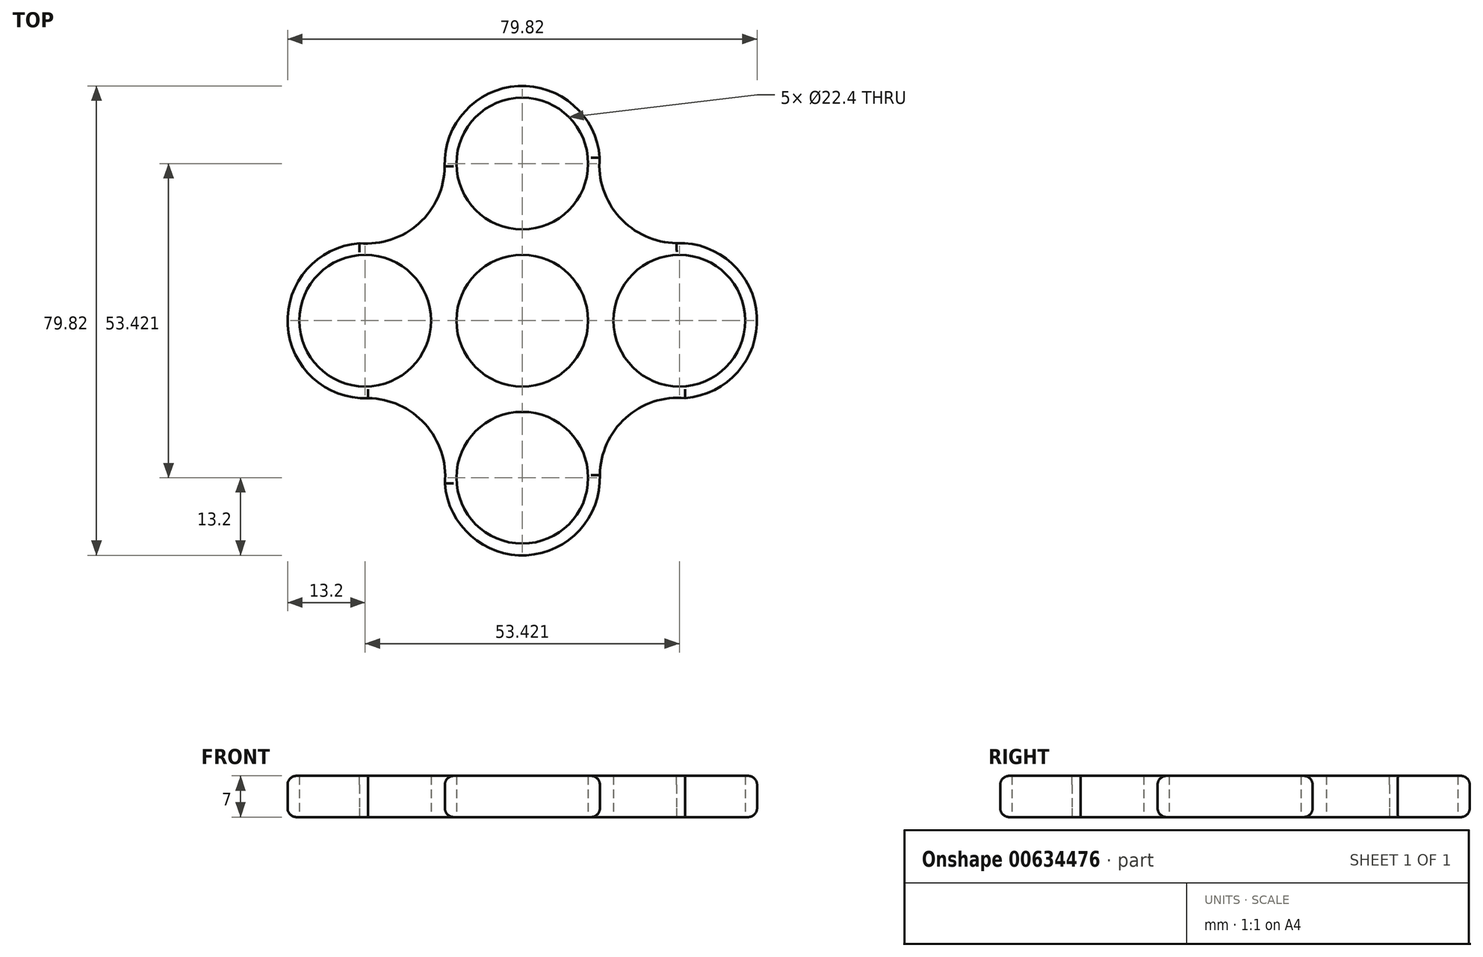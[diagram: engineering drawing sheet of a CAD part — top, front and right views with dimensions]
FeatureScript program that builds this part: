
annotation { "Feature Type Name" : "Feature", "Feature Type Description" : "" }
export const myFeature = defineFeature(function(context is Context, id is Id, definition is map)
    precondition{}
    {
        {
            var Q0;
            Q0=qCreatedBy(makeId("Top.planeOp"),FACE);
            var sketch = newSketch(context, id + "F0", { "sketchPlane" : qUnion([Q0])});
            skCircle(sketch, "E0", {"center": v(0, 0) * mm, "radius": 11.2 * mm});
            skCircle(sketch, "E1", {"center": v(0, 26.71) * mm, "radius": 11.2 * mm});
            skArc(sketch, "E2", {"start": v(13.14, 25.5) * mm, "mid": v(0.37, 39.9) * mm, "end": v(-13.2, 26.24) * mm});
            skCircle(sketch, "E3.1.0", {"center": v(-26.71, 0) * mm, "radius": 11.2 * mm});
            skArc(sketch, "E3.1.1", {"start": v(-25.5, 13.14) * mm, "mid": v(-39.9, 0.37) * mm, "end": v(-26.24, -13.2) * mm});
            skCircle(sketch, "E3.2.0", {"center": v(0, -26.71) * mm, "radius": 11.2 * mm});
            skArc(sketch, "E3.2.1", {"start": v(-13.14, -25.5) * mm, "mid": v(-0.37, -39.9) * mm, "end": v(13.2, -26.24) * mm});
            skCircle(sketch, "E3.3.0", {"center": v(26.71, 0) * mm, "radius": 11.2 * mm});
            skArc(sketch, "E3.3.1", {"start": v(25.5, -13.14) * mm, "mid": v(39.9, -0.37) * mm, "end": v(26.24, 13.2) * mm});
            skArc(sketch, "E4", {"start": v(13.16, 27.69) * mm, "mid": v(16.53, 17.58) * mm, "end": v(26.24, 13.2) * mm});
            skArc(sketch, "E5.1.0", {"start": v(-27.69, 13.16) * mm, "mid": v(-17.58, 16.53) * mm, "end": v(-13.2, 26.24) * mm});
            skArc(sketch, "E5.2.0", {"start": v(-13.16, -27.69) * mm, "mid": v(-16.53, -17.58) * mm, "end": v(-26.24, -13.2) * mm});
            skArc(sketch, "E5.3.0", {"start": v(27.69, -13.16) * mm, "mid": v(17.58, -16.53) * mm, "end": v(13.2, -26.24) * mm});
            skSolve(sketch);
        }
        {
            var Q0;
            Q0=makeQuery(id+"F0.imprint","IMPRINT",FACE,{"disambiguationData":[TD([[makeQuery(id+"F0.imprint","IMPRINT",EDGE,{"derivedFrom":sQuery(id+"F0.wireOp",EDGE,"E0")}),-1.0]])]});
            extrude(context, id + "F1", {"entities" : qUnion([Q0]), "depth" : 7 * mm, "offsetDistance" : 25 * mm});
        }
        {
            var Q0;
            Q0=makeQuery(id+"F1.opExtrude","CAP_EDGE",EDGE,{"disambiguationData":[OSD([sQuery(id+"F0.wireOp",EDGE,"E3.1.1")])],"isStart":true});
            var Q1;
            Q1=makeQuery(id+"F1.opExtrude","CAP_EDGE",EDGE,{"disambiguationData":[OSD([sQuery(id+"F0.wireOp",EDGE,"E5.2.0")])],"isStart":true});
            var Q2;
            Q2=makeQuery(id+"F1.opExtrude","CAP_EDGE",EDGE,{"disambiguationData":[OSD([sQuery(id+"F0.wireOp",EDGE,"E3.2.1")])],"isStart":true});
            var Q3;
            Q3=makeQuery(id+"F1.opExtrude","CAP_EDGE",EDGE,{"disambiguationData":[OSD([sQuery(id+"F0.wireOp",EDGE,"E5.3.0")])],"isStart":true});
            var Q4;
            Q4=makeQuery(id+"F1.opExtrude","CAP_EDGE",EDGE,{"disambiguationData":[OSD([sQuery(id+"F0.wireOp",EDGE,"E5.1.0")])],"isStart":true});
            var Q5;
            Q5=makeQuery(id+"F1.opExtrude","CAP_EDGE",EDGE,{"disambiguationData":[OSD([sQuery(id+"F0.wireOp",EDGE,"E2")])],"isStart":true});
            var Q6;
            Q6=makeQuery(id+"F1.opExtrude","CAP_EDGE",EDGE,{"disambiguationData":[OSD([sQuery(id+"F0.wireOp",EDGE,"E4")])],"isStart":true});
            var Q7;
            Q7=makeQuery(id+"F1.opExtrude","CAP_EDGE",EDGE,{"disambiguationData":[OSD([sQuery(id+"F0.wireOp",EDGE,"E3.3.1")])],"isStart":true});
            fillet(context, id + "F2", {"entities" : qUnion([Q0, Q1, Q2, Q3, Q4, Q5, Q6, Q7]), "radius" : 1.5 * mm, "tangentPropagation" : true, "allowEdgeOverflow" : false});
        }
        {
            var Q0;
            Q0=makeQuery(id+"F1.opExtrude","CAP_EDGE",EDGE,{"disambiguationData":[OSD([sQuery(id+"F0.wireOp",EDGE,"E3.1.1")])],"isStart":false});
            var Q1;
            Q1=makeQuery(id+"F1.opExtrude","CAP_EDGE",EDGE,{"disambiguationData":[OSD([sQuery(id+"F0.wireOp",EDGE,"E5.2.0")])],"isStart":false});
            var Q2;
            Q2=makeQuery(id+"F1.opExtrude","CAP_EDGE",EDGE,{"disambiguationData":[OSD([sQuery(id+"F0.wireOp",EDGE,"E3.2.1")])],"isStart":false});
            var Q3;
            Q3=makeQuery(id+"F1.opExtrude","CAP_EDGE",EDGE,{"disambiguationData":[OSD([sQuery(id+"F0.wireOp",EDGE,"E5.3.0")])],"isStart":false});
            var Q4;
            Q4=makeQuery(id+"F1.opExtrude","CAP_EDGE",EDGE,{"disambiguationData":[OSD([sQuery(id+"F0.wireOp",EDGE,"E5.1.0")])],"isStart":false});
            var Q5;
            Q5=makeQuery(id+"F1.opExtrude","CAP_EDGE",EDGE,{"disambiguationData":[OSD([sQuery(id+"F0.wireOp",EDGE,"E2")])],"isStart":false});
            var Q6;
            Q6=makeQuery(id+"F1.opExtrude","CAP_EDGE",EDGE,{"disambiguationData":[OSD([sQuery(id+"F0.wireOp",EDGE,"E4")])],"isStart":false});
            var Q7;
            Q7=makeQuery(id+"F1.opExtrude","CAP_EDGE",EDGE,{"disambiguationData":[OSD([sQuery(id+"F0.wireOp",EDGE,"E3.3.1")])],"isStart":false});
            fillet(context, id + "F3", {"entities" : qUnion([Q0, Q1, Q2, Q3, Q4, Q5, Q6, Q7]), "radius" : 1.5 * mm, "tangentPropagation" : true, "allowEdgeOverflow" : false});
        }
    });
